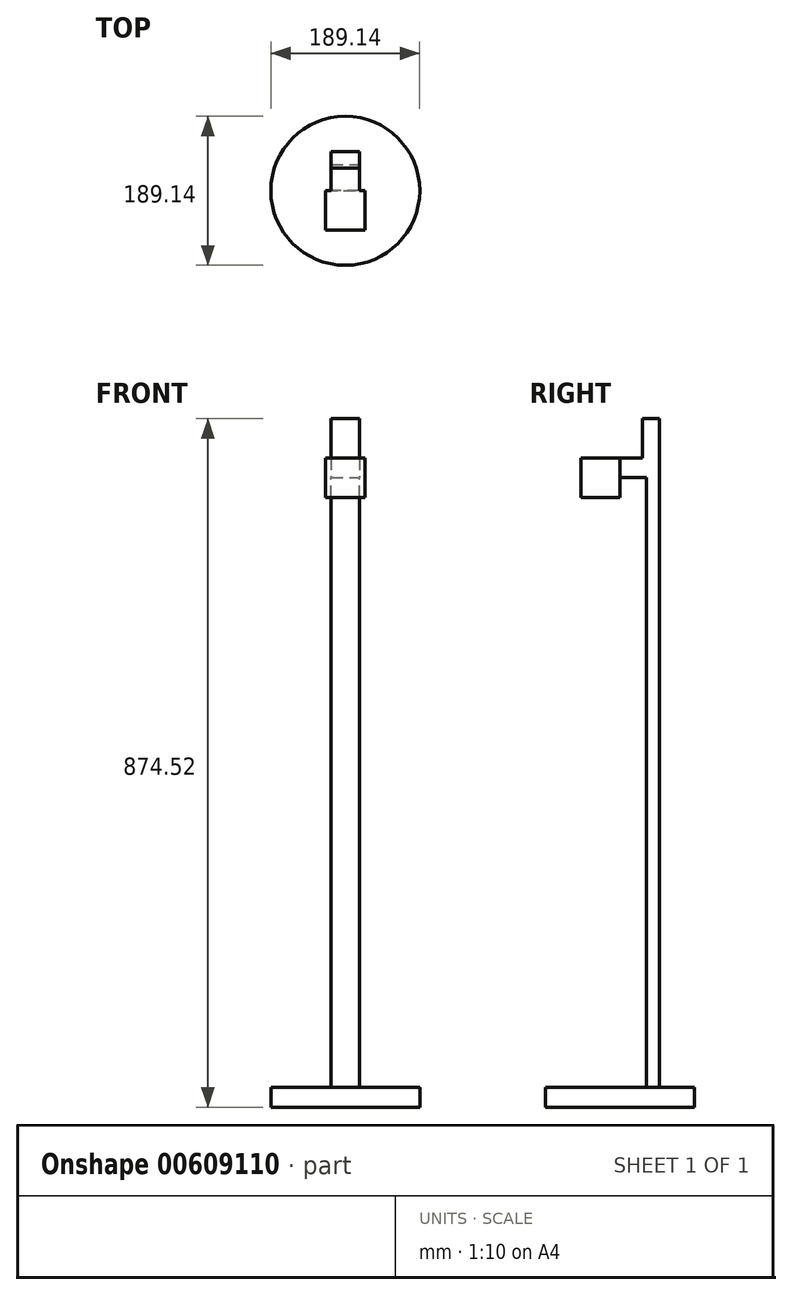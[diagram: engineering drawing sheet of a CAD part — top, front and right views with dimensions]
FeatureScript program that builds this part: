
annotation { "Feature Type Name" : "Feature", "Feature Type Description" : "" }
export const myFeature = defineFeature(function(context is Context, id is Id, definition is map)
    precondition{}
    {
        {
            var Q0;
            Q0=qCreatedBy(makeId("Front.planeOp"),FACE);
            var sketch = newSketch(context, id + "F0", { "sketchPlane" : qUnion([Q0])});
            skLineSegment(sketch, "E0.bottom", {"start": v(-25, 25) * mm, "end": v(25, 25) * mm});
            skLineSegment(sketch, "E0.top", {"start": v(-25, -25) * mm, "end": v(25, -25) * mm});
            skLineSegment(sketch, "E0.left", {"start": v(-25, 25) * mm, "end": v(-25, -25) * mm});
            skLineSegment(sketch, "E0.right", {"start": v(25, 25) * mm, "end": v(25, -25) * mm});
            skPoint(sketch, "E0.middle", {"position": v(0, 0) * mm});
            skSolve(sketch);
        }
        {
            var Q0;
            Q0=makeQuery(id+"F0.imprint","IMPRINT",FACE,{"disambiguationData":[TD([[makeQuery(id+"F0.imprint","IMPRINT",EDGE,{"derivedFrom":sQuery(id+"F0.wireOp",EDGE,"E0.bottom")}),-1.0]])]});
            extrude(context, id + "F1", {"entities" : qUnion([Q0]), "depth" : 50 * mm});
        }
        {
            var Q0;
            Q0=makeQuery(id+"F1.opExtrude","CAP_FACE",FACE,{"disambiguationData":[OSD([sQuery(id+"F0.wireOp",EDGE,"E0.bottom"),sQuery(id+"F0.wireOp",EDGE,"E0.top"),sQuery(id+"F0.wireOp",EDGE,"E0.left"),sQuery(id+"F0.wireOp",EDGE,"E0.right")])],"isStart":true});
            var sketch = newSketch(context, id + "F2", { "sketchPlane" : qUnion([Q0])});
            skLineSegment(sketch, "E1.bottom", {"start": v(-17.84, 25) * mm, "end": v(17.84, 25) * mm});
            skLineSegment(sketch, "E1.top", {"start": v(-17.84, 0.48) * mm, "end": v(17.84, 0.48) * mm});
            skLineSegment(sketch, "E1.left", {"start": v(-17.84, 25) * mm, "end": v(-17.84, 0.48) * mm});
            skLineSegment(sketch, "E1.right", {"start": v(17.84, 25) * mm, "end": v(17.84, 0.48) * mm});
            skPoint(sketch, "E1.middle", {"position": v(0, 12.74) * mm});
            skSolve(sketch);
        }
        {
            var Q0;
            Q0=makeQuery(id+"F2.imprint","IMPRINT",FACE,{"disambiguationData":[TD([[makeQuery(id+"F2.imprint","IMPRINT",EDGE,{"derivedFrom":sQuery(id+"F2.wireOp",EDGE,"E1.bottom")}),1.0]])]});
            var sketch = newSketch(context, id + "F3", { "sketchPlane" : qUnion([Q0])});
            skSolve(sketch);
        }
        {
            var Q0;
            Q0=qSketchRegion(id+"F3",true);
            var Q1;
            Q1=makeQuery(id+"F2.imprint","IMPRINT",FACE,{"disambiguationData":[TD([[makeQuery(id+"F2.imprint","IMPRINT",EDGE,{"derivedFrom":sQuery(id+"F2.wireOp",EDGE,"E1.bottom")}),1.0]])]});
            extrude(context, id + "F4", {"entities" : qUnion([Q0, Q1]), "operationType" : NewBodyOperationType.ADD, "depth" : 50 * mm});
        }
        {
            var Q0;
            Q0=makeQuery(id+"F4.boolean.opBoolean","MERGE",FACE,{"derivedFrom":[makeQuery(id+"F1.opExtrude","SWEPT_FACE",FACE,{"disambiguationData":[OSD([sQuery(id+"F0.wireOp",EDGE,"E0.bottom")])]}),makeQuery(id+"F4.opExtrude","SWEPT_FACE",FACE,{"disambiguationData":[OSD([sQuery(id+"F2.wireOp",EDGE,"E1.bottom")])]})]});
            var sketch = newSketch(context, id + "F5", { "sketchPlane" : qUnion([Q0])});
            skLineSegment(sketch, "E2.bottom", {"start": v(17.84, 50) * mm, "end": v(-17.84, 50) * mm});
            skLineSegment(sketch, "E2.top", {"start": v(17.84, 28.59) * mm, "end": v(-17.84, 28.59) * mm});
            skLineSegment(sketch, "E2.left", {"start": v(17.84, 50) * mm, "end": v(17.84, 28.59) * mm});
            skLineSegment(sketch, "E2.right", {"start": v(-17.84, 50) * mm, "end": v(-17.84, 28.59) * mm});
            skSolve(sketch);
        }
        {
            var Q0;
            Q0=makeQuery(id+"F5.imprint","IMPRINT",FACE,{"disambiguationData":[TD([[makeQuery(id+"F5.imprint","IMPRINT",EDGE,{"derivedFrom":sQuery(id+"F5.wireOp",EDGE,"E2.bottom")}),-1.0]])]});
            extrude(context, id + "F6", {"entities" : qUnion([Q0]), "operationType" : NewBodyOperationType.ADD, "depth" : 50 * mm});
        }
        {
            var Q0;
            Q0=makeQuery(id+"F4.opExtrude","SWEPT_FACE",FACE,{"disambiguationData":[OSD([sQuery(id+"F2.wireOp",EDGE,"E1.top")])]});
            var sketch = newSketch(context, id + "F7", { "sketchPlane" : qUnion([Q0])});
            skLineSegment(sketch, "E3.bottom", {"start": v(-17.84, -50) * mm, "end": v(17.84, -50) * mm});
            skLineSegment(sketch, "E3.top", {"start": v(-17.84, -33.39) * mm, "end": v(17.84, -33.39) * mm});
            skLineSegment(sketch, "E3.left", {"start": v(-17.84, -50) * mm, "end": v(-17.84, -33.39) * mm});
            skLineSegment(sketch, "E3.right", {"start": v(17.84, -50) * mm, "end": v(17.84, -33.39) * mm});
            skSolve(sketch);
        }
        {
            var Q0;
            Q0=makeQuery(id+"F7.imprint","IMPRINT",FACE,{"disambiguationData":[TD([[makeQuery(id+"F7.imprint","IMPRINT",EDGE,{"derivedFrom":sQuery(id+"F7.wireOp",EDGE,"E3.bottom")}),-1.0]])]});
            extrude(context, id + "F8", {"entities" : qUnion([Q0]), "operationType" : NewBodyOperationType.ADD, "depth" : 800 * mm});
        }
        {
            var Q0;
            Q0=makeQuery(id+"F8.opExtrude","CAP_FACE",FACE,{"disambiguationData":[OSD([sQuery(id+"F7.wireOp",EDGE,"E3.bottom"),sQuery(id+"F7.wireOp",EDGE,"E3.top"),sQuery(id+"F7.wireOp",EDGE,"E3.left"),sQuery(id+"F7.wireOp",EDGE,"E3.right")])],"isStart":false});
            var sketch = newSketch(context, id + "F9", { "sketchPlane" : qUnion([Q0])});
            skCircle(sketch, "E4", {"center": v(0, 0) * mm, "radius": 94.57 * mm});
            skSolve(sketch);
        }
        {
            var Q0;
            Q0=makeQuery(id+"F9.imprint","IMPRINT",FACE,{"disambiguationData":[TD([[makeQuery(id+"F9.imprint","IMPRINT",EDGE,{"derivedFrom":sQuery(id+"F9.wireOp",EDGE,"E4")}),1.0]])]});
            var sketch = newSketch(context, id + "F10", { "sketchPlane" : qUnion([Q0])});
            skSolve(sketch);
        }
        {
            var Q0;
            Q0=qSketchRegion(id+"F10",true);
            var Q1;
            Q1=makeQuery(id+"F9.imprint","IMPRINT",FACE,{"disambiguationData":[TD([[makeQuery(id+"F9.imprint","IMPRINT",EDGE,{"derivedFrom":sQuery(id+"F9.wireOp",EDGE,"E4")}),1.0]])]});
            extrude(context, id + "F11", {"entities" : qUnion([Q0, Q1]), "operationType" : NewBodyOperationType.ADD, "oppositeDirection" : true, "depth" : 25 * mm});
        }
    });
